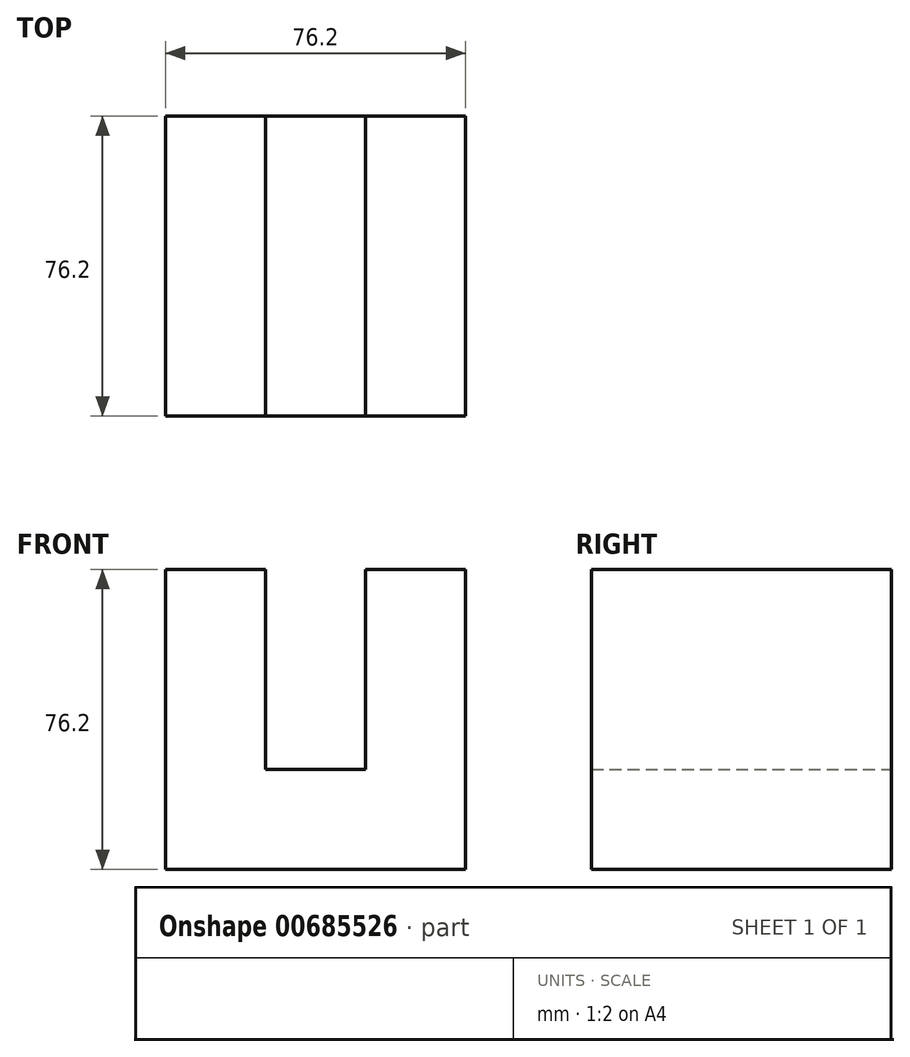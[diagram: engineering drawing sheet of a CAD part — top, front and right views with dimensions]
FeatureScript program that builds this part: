
annotation { "Feature Type Name" : "Feature", "Feature Type Description" : "" }
export const myFeature = defineFeature(function(context is Context, id is Id, definition is map)
    precondition{}
    {
        {
            var Q0;
            Q0=qCreatedBy(makeId("Front.planeOp"),FACE);
            var sketch = newSketch(context, id + "F0", { "sketchPlane" : qUnion([Q0])});
            skLineSegment(sketch, "E0", {"start": v(0, 0) * mm, "end": v(0, -76.2) * mm});
            skLineSegment(sketch, "E1", {"start": v(0, -76.2) * mm, "end": v(76.2, -76.2) * mm});
            skLineSegment(sketch, "E2", {"start": v(76.2, -76.2) * mm, "end": v(76.2, 0) * mm});
            skLineSegment(sketch, "E3", {"start": v(76.2, 0) * mm, "end": v(50.8, 0) * mm});
            skLineSegment(sketch, "E4", {"start": v(50.8, 0) * mm, "end": v(50.8, -50.8) * mm});
            skLineSegment(sketch, "E5", {"start": v(50.8, -50.8) * mm, "end": v(25.4, -50.8) * mm});
            skLineSegment(sketch, "E6", {"start": v(25.4, -50.8) * mm, "end": v(25.4, 0) * mm});
            skLineSegment(sketch, "E7", {"start": v(25.4, 0) * mm, "end": v(0, 0) * mm});
            skSolve(sketch);
        }
        {
            var Q0;
            Q0 = qSketchRegion(id + "F0", true);
            extrude(context, id + "F1", {"entities" : qUnion([Q0]), "depth" : 76.2 * mm, "offsetDistance" : 25.4 * mm});
        }
    });
